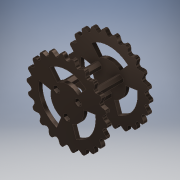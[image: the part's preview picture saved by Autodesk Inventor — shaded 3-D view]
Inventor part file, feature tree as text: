
AUTODESK INVENTOR PART (.ipt)
format: ipt  version: 2019 (Build 230136000, 136)  size: 499,200 bytes
history: native  units: mm
features: extrude x5, sketch x5, pattern_circular x2, projected_geometry x1
ambient origin geometry x8: Origin, YZ Plane, XZ Plane, XY Plane, X Axis, Y Axis, Z Axis, Center Point
bodies: Solid1 (feature_tree)
feature tree (13):
  extrude  "Extrusion1"  Depth=2.5mm TaperAngle=0.0deg
  extrude  "Extrusion2"  Depth=2.5mm TaperAngle=0.0deg
  pattern_circular  "Circular Pattern1"  Count=22 Angle=360.0deg
  extrude  "Extrusion3"  Depth=2.5mm TaperAngle=360.0deg
  pattern_circular  "Circular Pattern2"  [2 undecoded]
  extrude  "Extrusion4"  Depth=4.0mm
  extrude  "Extrusion5"  Depth=2.5mm TaperAngle=360.0deg
  sketch  "Sketch1"  dims[d0=55.0mm d1=2.5mm d2=0.0mm]
  sketch  "Sketch2"  dims[d3=49.0mm d4=2.5mm d5=0.0mm d6=220.0mm d7=360.0deg]
  sketch  "Sketch3"  dims[d10=2.5mm d11=0.0mm d12=30.0mm d13=360.0deg]
  sketch  "Sketch4"  dims[d15=3.0mm]
  sketch  "Sketch5"  dims[d16=3.490659mm d17=8.5mm d18=4.0mm d19=30.0mm d21=360.0deg d23=26.0mm d24=0.0mm d25=2.5mm d26=0.0mm]
  projected_geometry  "Projected Loop1"
note: 2 required parameter values undecoded (feature->parameter linkage not recoverable at this tier; creation-order binding heuristic only, values carry confidence <= 0.55)
